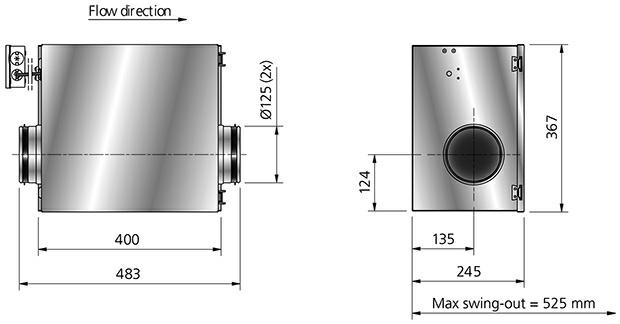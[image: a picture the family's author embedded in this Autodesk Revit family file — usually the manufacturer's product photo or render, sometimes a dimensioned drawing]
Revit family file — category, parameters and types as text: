
# Revit family: IRE 315 B3 ErP AC_7900240
name_source: partatom
category: Mechanical Equipment
revit_build: Autodesk Revit MEP 2014 (Build: 20130308_1515(x64)
units: mm (PartAtom-declared; Revit-internal decimal feet)

## types (1)
- IRE 315 B3 ErP AC
    Capacitor = - μF
    Current = 1 A
    Depth = 587 mm  [stored 1.92585 ft]
    Description = Insulated duct fans with circular connections
    Diameter = 315 mm  [stored 1.03346 ft]
    Frequency = 50 Hz
    Height = 396 mm  [stored 1.29921 ft]
    Main Material = Steel, Galvanized
    Max. temperature of transported air = 60 °C
    Max. temperature of transported air when speed controlled = 60 °C
    Phase = 3
    Power = 638 W
    Sound pressure level at 3 m = 47 dB(A)
    Speed = 1290 rpm
    Voltage = 400 V
    Voltage range = 380-415 V
    Weight = 30.70 kg
    Width = 727 mm  [stored 2.38517 ft]
    Wiring diagram = Y 4040004 / Δ 4040003

note: [stored X ft] marks values corroborated as IEEE doubles in the binary element streams (Revit-internal decimal feet)

## geometry (parser evidence)
native form markers: Sweep x5
no freeform markers — native parametric forms only
